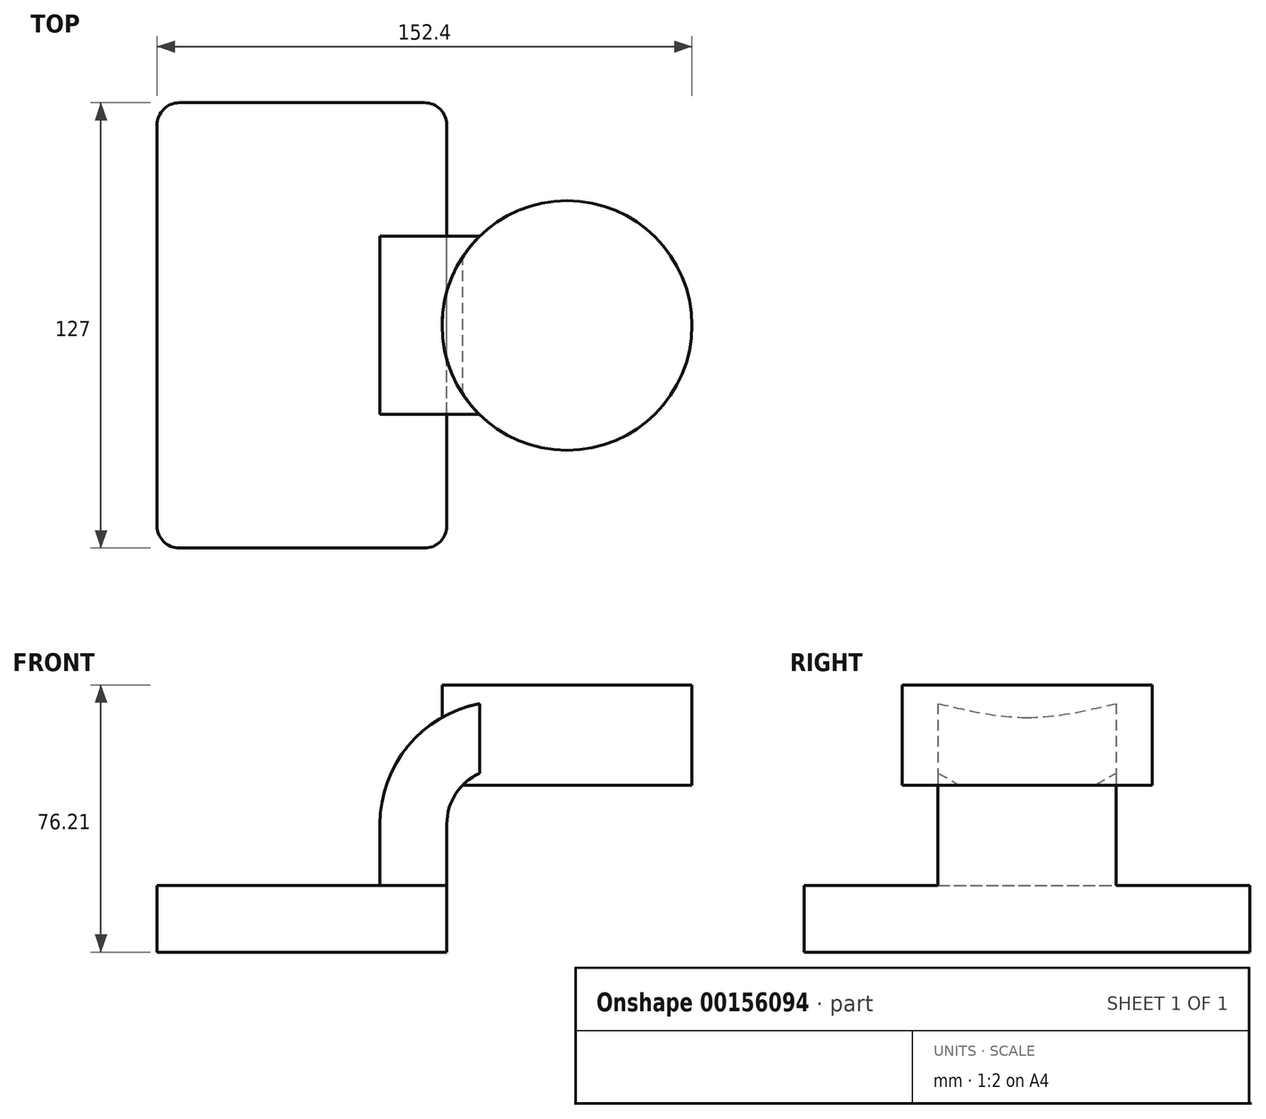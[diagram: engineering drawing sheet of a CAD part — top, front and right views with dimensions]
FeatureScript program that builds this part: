
annotation { "Feature Type Name" : "Feature", "Feature Type Description" : "" }
export const myFeature = defineFeature(function(context is Context, id is Id, definition is map)
    precondition{}
    {
        {
            var Q0;
            Q0=qCreatedBy(makeId("Front.planeOp"),FACE);
            var sketch = newSketch(context, id + "F0", { "sketchPlane" : qUnion([Q0])});
            skLineSegment(sketch, "E0.bottom", {"start": v(41.28, -9.52) * mm, "end": v(-41.28, -9.53) * mm});
            skLineSegment(sketch, "E0.top", {"start": v(41.28, 9.53) * mm, "end": v(-41.28, 9.52) * mm});
            skLineSegment(sketch, "E0.left", {"start": v(41.28, -9.52) * mm, "end": v(41.28, 9.53) * mm});
            skLineSegment(sketch, "E0.right", {"start": v(-41.28, -9.53) * mm, "end": v(-41.28, 9.52) * mm});
            skPoint(sketch, "E0.middle", {"position": v(0, 0) * mm});
            skLineSegment(sketch, "E1.bottom", {"start": v(60.32, 38.1) * mm, "end": v(111.12, 38.1) * mm});
            skLineSegment(sketch, "E1.top", {"start": v(60.32, 66.67) * mm, "end": v(111.12, 66.67) * mm});
            skLineSegment(sketch, "E1.left", {"start": v(60.32, 38.1) * mm, "end": v(60.32, 66.68) * mm});
            skLineSegment(sketch, "E1.right", {"start": v(111.12, 38.1) * mm, "end": v(111.12, 66.68) * mm});
            skPoint(sketch, "E1.middle", {"position": v(85.72, 52.39) * mm});
            skLineSegment(sketch, "E2", {"start": v(41.28, 9.53) * mm, "end": v(41.28, 27) * mm});
            skArc(sketch, "E3", {"start": v(41.28, 27) * mm, "mid": v(45.92, 38.23) * mm, "end": v(57.15, 42.88) * mm});
            skLineSegment(sketch, "E4", {"start": v(57.15, 42.88) * mm, "end": v(75.53, 42.88) * mm});
            skLineSegment(sketch, "E5.0", {"start": v(57.15, 61.93) * mm, "end": v(75.53, 61.93) * mm});
            skArc(sketch, "E5.1", {"start": v(22.23, 27) * mm, "mid": v(32.45, 51.7) * mm, "end": v(57.15, 61.93) * mm});
            skLineSegment(sketch, "E5.2", {"start": v(22.23, 9.53) * mm, "end": v(22.23, 27) * mm});
            skLineSegment(sketch, "E6", {"start": v(75.53, 38.1) * mm, "end": v(75.53, 66.67) * mm});
            skFitSpline(sketch, "E7", {"points": [v(-41.28, 9.52) * mm, v(57.15, 61.93) * mm], "startDerivative": vector(2.53, 73.97) * mm, "endDerivative": vector(131.97, -0.16) * mm});
            skSolve(sketch);
        }
        {
            var Q0;
            Q0=makeQuery(id+"F0.imprint","IMPRINT",FACE,{"disambiguationData":[TD([[makeQuery(id+"F0.imprint","IMPRINT",EDGE,{"derivedFrom":sQuery(id+"F0.wireOp",EDGE,"E0.bottom")}),-1.0]])]});
            extrude(context, id + "F1", {"entities" : qUnion([Q0]), "endBound" : BoundingType.SYMMETRIC, "depth" : 127 * mm});
        }
        {
            var Q0;
            {var subQ1=sQuery(id+"F0.wireOp",EDGE,"E2");Q0=makeQuery(id+"F0.imprint","IMPRINT",FACE,{"disambiguationData":[TD([[makeQuery(id+"F0.imprint","IMPRINT",EDGE,{"derivedFrom":subQ1}),1.0]])]});}
            var Q1;
            {var subQ0=sQuery(id+"F0.wireOp",EDGE,"E4");var subQ1=sQuery(id+"F0.wireOp",EDGE,"E1.left");var subQ2=makeQuery(id+"F0.imprint","INTERSECT",VERTEX,{"derivedFrom":[subQ1,subQ0]});Q1=makeQuery(id+"F0.imprint","IMPRINT",FACE,{"disambiguationData":[TD([[makeQuery(id+"F0.imprint","IMPRINT",EDGE,{"disambiguationData":[TD([[subQ2,-1.0]])],"derivedFrom":subQ1}),-1.0]])]});}
            extrude(context, id + "F2", {"entities" : qUnion([Q0, Q1]), "operationType" : NewBodyOperationType.ADD, "endBound" : BoundingType.SYMMETRIC, "depth" : 50.8 * mm});
        }
        {
            var Q0;
            Q0=makeQuery(id+"F0.imprint","IMPRINT",FACE,{"disambiguationData":[TD([[makeQuery(id+"F0.imprint","IMPRINT",EDGE,{"derivedFrom":sQuery(id+"F0.wireOp",EDGE,"E5.1")}),1.0]])]});
            extrude(context, id + "F3", {"entities" : qUnion([Q0]), "operationType" : NewBodyOperationType.ADD, "endBound" : BoundingType.SYMMETRIC, "depth" : 15.88 * mm});
        }
        {
            var Q0;
            {var subQ0=sQuery(id+"F0.wireOp",EDGE,"E1.right");Q0=makeQuery(id+"F0.imprint","IMPRINT",FACE,{"disambiguationData":[TD([[makeQuery(id+"F0.imprint","IMPRINT",EDGE,{"derivedFrom":subQ0}),1.0]])]});}
            var Q1;
            Q1=sQuery(id+"F0.wireOp",EDGE,"E6");
            revolve(context, id + "F4", {"operationType" : NewBodyOperationType.ADD, "entities" : qUnion([Q0]), "axis" : qUnion([Q1]), "revolveType" : RevolveType.FULL});
        }
        {
            var Q0;
            Q0=makeQuery(id+"F1.opExtrude","CAP_EDGE",EDGE,{"disambiguationData":[OSD([sQuery(id+"F0.wireOp",EDGE,"E0.right")])],"isStart":false});
            var Q1;
            Q1=makeQuery(id+"F1.opExtrude","CAP_EDGE",EDGE,{"disambiguationData":[OSD([sQuery(id+"F0.wireOp",EDGE,"E0.left")])],"isStart":false});
            var Q2;
            Q2=makeQuery(id+"F1.opExtrude","CAP_EDGE",EDGE,{"disambiguationData":[OSD([sQuery(id+"F0.wireOp",EDGE,"E0.left")])],"isStart":true});
            var Q3;
            Q3=makeQuery(id+"F1.opExtrude","CAP_EDGE",EDGE,{"disambiguationData":[OSD([sQuery(id+"F0.wireOp",EDGE,"E0.right")])],"isStart":true});
            fillet(context, id + "F5", {"entities" : qUnion([Q0, Q1, Q2, Q3]), "radius" : 6.35 * mm, "tangentPropagation" : true, "allowEdgeOverflow" : false});
        }
    });
